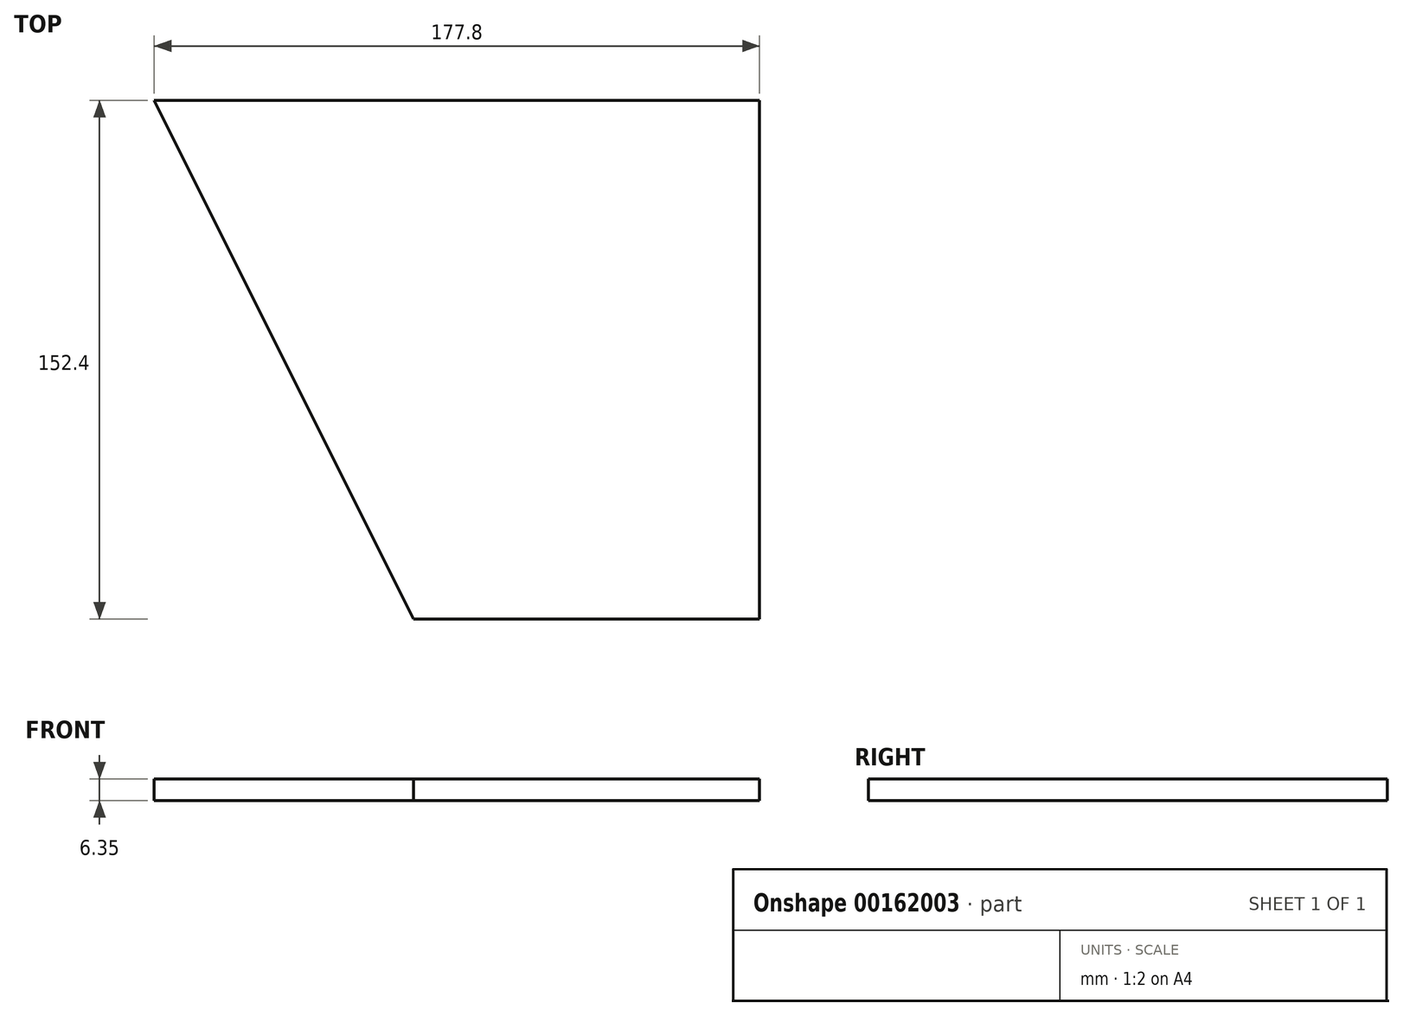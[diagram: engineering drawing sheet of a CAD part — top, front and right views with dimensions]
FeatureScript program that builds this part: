
annotation { "Feature Type Name" : "Feature", "Feature Type Description" : "" }
export const myFeature = defineFeature(function(context is Context, id is Id, definition is map)
    precondition{}
    {
        {
            var Q0;
            Q0=qCreatedBy(makeId("Top.planeOp"),FACE);
            var sketch = newSketch(context, id + "F0", { "sketchPlane" : qUnion([Q0])});
            skLineSegment(sketch, "E0", {"start": v(122.34, -17.87) * mm, "end": v(20.74, -17.87) * mm});
            skLineSegment(sketch, "E1", {"start": v(122.34, -17.87) * mm, "end": v(122.34, 134.53) * mm});
            skLineSegment(sketch, "E2", {"start": v(122.34, 134.53) * mm, "end": v(-55.46, 134.53) * mm});
            skLineSegment(sketch, "E3", {"start": v(-55.46, 134.53) * mm, "end": v(20.74, -17.87) * mm});
            skSolve(sketch);
        }
        {
            var Q0;
            Q0=makeQuery(id+"F0.imprint","IMPRINT",FACE,{"disambiguationData":[TD([[makeQuery(id+"F0.imprint","IMPRINT",EDGE,{"derivedFrom":sQuery(id+"F0.wireOp",EDGE,"E0")}),-1.0]])]});
            extrude(context, id + "F1", {"entities" : qUnion([Q0]), "depth" : 6.35 * mm});
        }
    });
